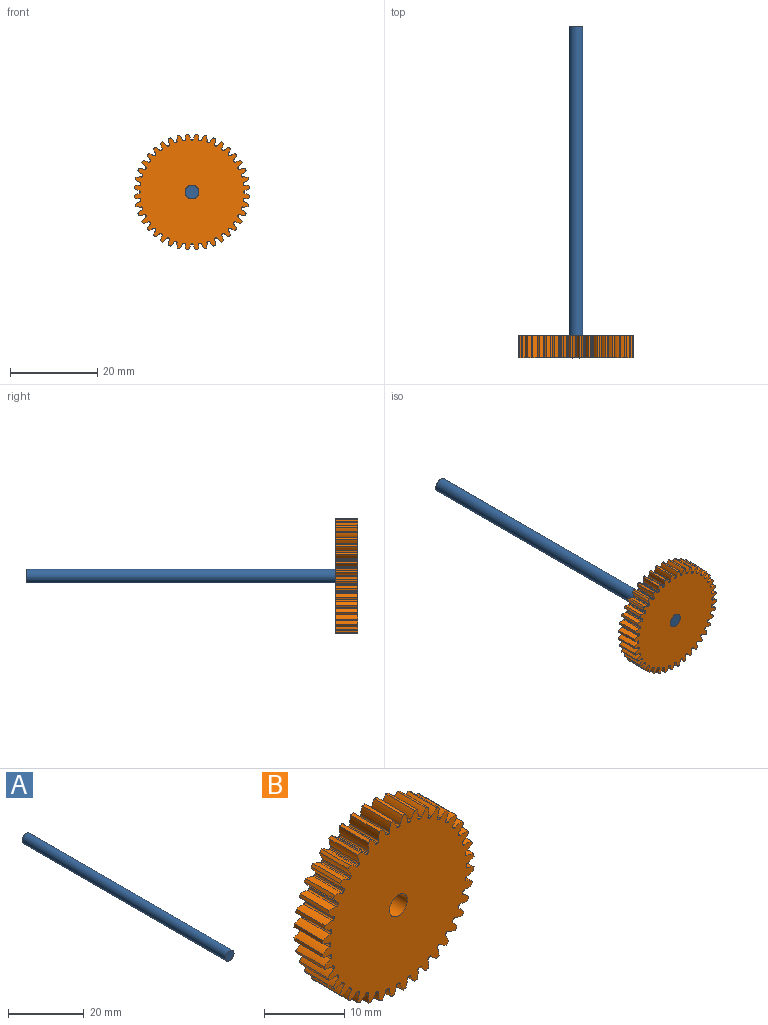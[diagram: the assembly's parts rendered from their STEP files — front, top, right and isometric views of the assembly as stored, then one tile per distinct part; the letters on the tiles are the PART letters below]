
ASSEMBLY  parts=2 mates=1
PART A: 3 faces, bbox 3.2x76.2x3.2 mm
  f0: cylinder r=1.59mm len=76.2mm, axis (0,1,0), area 760.1mm2, adj f1,f2
  f1: plane 3.18x3.18mm, normal (0,-1,0), area 7.9mm2, adj f0
  f2: plane 3.18x3.18mm, normal (0,1,0), area 7.9mm2, adj f0
PART B: 243 faces, bbox 26.6x5.1x26.6 mm
  f0: cylinder r=13.33mm len=5.08mm, axis (0,1,0), area 2.5mm2, adj f39,f41,f147,f239
  f1: cylinder r=13.33mm len=5.08mm, axis (0,1,0), area 2.5mm2, adj f39,f41,f234,f237
  f2: cylinder r=13.33mm len=5.08mm, axis (0,1,0), area 2.5mm2, adj f39,f41,f229,f232
  f3: cylinder r=13.33mm len=5.08mm, axis (0,1,0), area 2.5mm2, adj f39,f41,f224,f227
  f4: cylinder r=13.33mm len=5.08mm, axis (0,1,0), area 2.5mm2, adj f39,f41,f219,f222
  f5: cylinder r=13.33mm len=5.08mm, axis (0,1,0), area 2.5mm2, adj f39,f41,f214,f217
  f6: cylinder r=13.33mm len=5.08mm, axis (0,1,0), area 2.5mm2, adj f39,f41,f209,f212
  f7: cylinder r=13.33mm len=5.08mm, axis (0,1,0), area 2.5mm2, adj f39,f41,f204,f207
  f8: cylinder r=13.33mm len=5.08mm, axis (0,1,0), area 2.5mm2, adj f39,f41,f192,f199
  f9: cylinder r=13.33mm len=5.08mm, axis (0,1,0), area 2.5mm2, adj f39,f41,f194,f202
  f10: cylinder r=13.33mm len=5.08mm, axis (0,1,0), area 2.5mm2, adj f39,f41,f189,f197
  f11: cylinder r=13.33mm len=5.08mm, axis (0,1,0), area 2.5mm2, adj f39,f41,f184,f187
  f12: cylinder r=13.33mm len=5.08mm, axis (0,1,0), area 2.5mm2, adj f39,f41,f179,f182
  f13: cylinder r=13.33mm len=5.08mm, axis (0,1,0), area 2.5mm2, adj f39,f41,f174,f177
  f14: cylinder r=13.33mm len=5.08mm, axis (0,1,0), area 2.5mm2, adj f39,f41,f169,f172
  f15: cylinder r=13.33mm len=5.08mm, axis (0,1,0), area 2.5mm2, adj f39,f41,f164,f167
  f16: cylinder r=13.33mm len=5.08mm, axis (0,1,0), area 2.5mm2, adj f39,f41,f137,f159
  f17: cylinder r=13.33mm len=5.08mm, axis (0,1,0), area 2.5mm2, adj f39,f41,f154,f157
  f18: cylinder r=13.33mm len=5.08mm, axis (0,1,0), area 2.5mm2, adj f39,f41,f142,f149
  f19: cylinder r=13.33mm len=5.08mm, axis (0,1,0), area 2.5mm2, adj f39,f41,f144,f152
  f20: cylinder r=13.33mm len=5.08mm, axis (0,1,0), area 2.5mm2, adj f39,f41,f132,f139
  f21: cylinder r=13.33mm len=5.08mm, axis (0,1,0), area 2.5mm2, adj f39,f41,f127,f134
  f22: cylinder r=13.33mm len=5.08mm, axis (0,1,0), area 2.5mm2, adj f39,f41,f122,f129
  f23: cylinder r=13.33mm len=5.08mm, axis (0,1,0), area 2.5mm2, adj f39,f41,f82,f124
  f24: cylinder r=13.33mm len=5.08mm, axis (0,1,0), area 2.5mm2, adj f39,f41,f42,f119
  f25: cylinder r=13.33mm len=5.08mm, axis (0,1,0), area 2.5mm2, adj f39,f41,f114,f117
  f26: cylinder r=13.33mm len=5.08mm, axis (0,1,0), area 2.5mm2, adj f39,f41,f109,f112
  f27: cylinder r=13.33mm len=5.08mm, axis (0,1,0), area 2.5mm2, adj f39,f41,f104,f107
  f28: cylinder r=13.33mm len=5.08mm, axis (0,1,0), area 2.5mm2, adj f39,f41,f92,f99
  f29: cylinder r=13.33mm len=5.08mm, axis (0,1,0), area 2.5mm2, adj f39,f41,f94,f102
  f30: cylinder r=13.33mm len=5.08mm, axis (0,1,0), area 2.5mm2, adj f39,f41,f89,f97
  f31: cylinder r=13.33mm len=5.08mm, axis (0,1,0), area 2.5mm2, adj f39,f41,f84,f87
  f32: cylinder r=13.33mm len=5.08mm, axis (0,1,0), area 2.5mm2, adj f39,f41,f67,f79
  f33: cylinder r=13.33mm len=5.08mm, axis (0,1,0), area 2.5mm2, adj f39,f41,f74,f77
  f34: cylinder r=13.33mm len=5.08mm, axis (0,1,0), area 2.5mm2, adj f39,f41,f62,f69
  f35: cylinder r=13.33mm len=5.08mm, axis (0,1,0), area 2.5mm2, adj f39,f41,f64,f162
  f36: cylinder r=13.33mm len=5.08mm, axis (0,1,0), area 2.5mm2, adj f39,f41,f59,f72
  f37: cylinder r=13.33mm len=5.08mm, axis (0,1,0), area 2.5mm2, adj f39,f41,f54,f57
  f38: cylinder r=13.33mm len=5.08mm, axis (0,1,0), area 2.5mm2, adj f39,f41,f49,f52
  f39: plane 26.62x26.62mm, normal (0,-1,0), area 495mm2, adj f0,f1,f2,f3,f4,f5,f6,f7
  f40: cylinder r=13.33mm len=5.08mm, axis (0,1,0), area 2.5mm2, adj f39,f41,f44,f47
  f41: plane 26.62x26.62mm, normal (0,1,0), area 495mm2, adj f0,f1,f2,f3,f4,f5,f6,f7
  f42: extruded ~5.08x1.22mm, area 6.7mm2, adj f24,f39,f41,f45
  f43: cylinder r=11.91mm len=5.08mm, axis (0,1,0), area 0.9mm2, adj f39,f41,f45,f46
  f44: extruded ~5.08x1.22mm, area 6.7mm2, adj f39,f40,f41,f46
  f45: cylinder r=0.22mm len=5.08mm, axis (0,1,0), area 1.6mm2, adj f39,f41,f42,f43
  f46: cylinder r=0.22mm len=5.08mm, axis (0,1,0), area 1.6mm2, adj f39,f41,f43,f44
  f47: extruded ~5.08x1.28mm, area 6.7mm2, adj f39,f40,f41,f50
  f48: cylinder r=11.91mm len=5.08mm, axis (0,1,0), area 0.9mm2, adj f39,f41,f50,f51
  f49: extruded ~5.08x1.13mm, area 6.7mm2, adj f38,f39,f41,f51
  f50: cylinder r=0.22mm len=5.08mm, axis (0,1,0), area 1.6mm2, adj f39,f41,f47,f48
  f51: cylinder r=0.22mm len=5.08mm, axis (0,1,0), area 1.6mm2, adj f39,f41,f48,f49
  f52: extruded ~5.08x1.31mm, area 6.7mm2, adj f38,f39,f41,f55
  f53: cylinder r=11.91mm len=5.08mm, axis (0,1,0), area 0.9mm2, adj f39,f41,f55,f56
  f54: extruded ~5.08x1.01mm, area 6.7mm2, adj f37,f39,f41,f56
  f55: cylinder r=0.22mm len=5.08mm, axis (0,1,0), area 1.6mm2, adj f39,f41,f52,f53
  f56: cylinder r=0.22mm len=5.08mm, axis (0,1,0), area 1.6mm2, adj f39,f41,f53,f54
  f57: extruded ~5.08x1.31mm, area 6.7mm2, adj f37,f39,f41,f60
  f58: cylinder r=11.91mm len=5.08mm, axis (0,1,0), area 0.9mm2, adj f39,f41,f60,f61
  f59: extruded ~5.08x0.99mm, area 6.7mm2, adj f36,f39,f41,f61
  f60: cylinder r=0.22mm len=5.08mm, axis (0,1,0), area 1.6mm2, adj f39,f41,f57,f58
  f61: cylinder r=0.22mm len=5.08mm, axis (0,1,0), area 1.6mm2, adj f39,f41,f58,f59
  f62: extruded ~5.08x0.99mm, area 6.7mm2, adj f34,f39,f41,f65
  f63: cylinder r=11.91mm len=5.08mm, axis (0,1,0), area 0.9mm2, adj f39,f41,f65,f66
  f64: extruded ~5.08x1.31mm, area 6.7mm2, adj f35,f39,f41,f66
  f65: cylinder r=0.22mm len=5.08mm, axis (0,1,0), area 1.6mm2, adj f39,f41,f62,f63
  f66: cylinder r=0.22mm len=5.08mm, axis (0,1,0), area 1.6mm2, adj f39,f41,f63,f64
  f67: extruded ~5.08x1.12mm, area 6.7mm2, adj f32,f39,f41,f70
  f68: cylinder r=11.91mm len=5.08mm, axis (0,1,0), area 0.9mm2, adj f39,f41,f70,f71
  f69: extruded ~5.08x1.28mm, area 6.7mm2, adj f34,f39,f41,f71
  f70: cylinder r=0.22mm len=5.08mm, axis (0,1,0), area 1.6mm2, adj f39,f41,f67,f68
  f71: cylinder r=0.22mm len=5.08mm, axis (0,1,0), area 1.6mm2, adj f39,f41,f68,f69
  f72: extruded ~5.08x1.28mm, area 6.7mm2, adj f36,f39,f41,f75
  f73: cylinder r=11.91mm len=5.08mm, axis (0,1,0), area 0.9mm2, adj f39,f41,f75,f76
  f74: extruded ~5.08x1.12mm, area 6.7mm2, adj f33,f39,f41,f76
  f75: cylinder r=0.22mm len=5.08mm, axis (0,1,0), area 1.6mm2, adj f39,f41,f72,f73
  f76: cylinder r=0.22mm len=5.08mm, axis (0,1,0), area 1.6mm2, adj f39,f41,f73,f74
  f77: extruded ~5.08x1.21mm, area 6.7mm2, adj f33,f39,f41,f80
  f78: cylinder r=11.91mm len=5.08mm, axis (0,1,0), area 0.9mm2, adj f39,f41,f80,f81
  f79: extruded ~5.08x1.21mm, area 6.7mm2, adj f32,f39,f41,f81
  f80: cylinder r=0.22mm len=5.08mm, axis (0,1,0), area 1.6mm2, adj f39,f41,f77,f78
  f81: cylinder r=0.22mm len=5.08mm, axis (0,1,0), area 1.6mm2, adj f39,f41,f78,f79
  f82: extruded ~5.08x1.31mm, area 6.7mm2, adj f23,f39,f41,f85
  f83: cylinder r=11.91mm len=5.08mm, axis (0,1,0), area 0.9mm2, adj f39,f41,f85,f86
  f84: extruded ~5.08x1.01mm, area 6.7mm2, adj f31,f39,f41,f86
  f85: cylinder r=0.22mm len=5.08mm, axis (0,1,0), area 1.6mm2, adj f39,f41,f82,f83
  f86: cylinder r=0.22mm len=5.08mm, axis (0,1,0), area 1.6mm2, adj f39,f41,f83,f84
  f87: extruded ~5.08x1.31mm, area 6.7mm2, adj f31,f39,f41,f90
  f88: cylinder r=11.91mm len=5.08mm, axis (0,1,0), area 0.9mm2, adj f39,f41,f90,f91
  f89: extruded ~5.08x0.99mm, area 6.7mm2, adj f30,f39,f41,f91
  f90: cylinder r=0.22mm len=5.08mm, axis (0,1,0), area 1.6mm2, adj f39,f41,f87,f88
  f91: cylinder r=0.22mm len=5.08mm, axis (0,1,0), area 1.6mm2, adj f39,f41,f88,f89
  f92: extruded ~5.08x1.21mm, area 6.7mm2, adj f28,f39,f41,f95
  f93: cylinder r=11.91mm len=5.08mm, axis (0,1,0), area 0.9mm2, adj f39,f41,f95,f96
  f94: extruded ~5.08x1.21mm, area 6.7mm2, adj f29,f39,f41,f96
  f95: cylinder r=0.22mm len=5.08mm, axis (0,1,0), area 1.6mm2, adj f39,f41,f92,f93
  f96: cylinder r=0.22mm len=5.08mm, axis (0,1,0), area 1.6mm2, adj f39,f41,f93,f94
  f97: extruded ~5.08x1.28mm, area 6.7mm2, adj f30,f39,f41,f100
  f98: cylinder r=11.91mm len=5.08mm, axis (0,1,0), area 0.9mm2, adj f39,f41,f100,f101
  f99: extruded ~5.08x1.12mm, area 6.7mm2, adj f28,f39,f41,f101
  f100: cylinder r=0.22mm len=5.08mm, axis (0,1,0), area 1.6mm2, adj f39,f41,f97,f98
  f101: cylinder r=0.22mm len=5.08mm, axis (0,1,0), area 1.6mm2, adj f39,f41,f98,f99
  f102: extruded ~5.08x1.12mm, area 6.7mm2, adj f29,f39,f41,f105
  f103: cylinder r=11.91mm len=5.08mm, axis (0,1,0), area 0.9mm2, adj f39,f41,f105,f106
  f104: extruded ~5.08x1.28mm, area 6.7mm2, adj f27,f39,f41,f106
  f105: cylinder r=0.22mm len=5.08mm, axis (0,1,0), area 1.6mm2, adj f39,f41,f102,f103
  f106: cylinder r=0.22mm len=5.08mm, axis (0,1,0), area 1.6mm2, adj f39,f41,f103,f104
  f107: extruded ~5.08x0.99mm, area 6.7mm2, adj f27,f39,f41,f110
  f108: cylinder r=11.91mm len=5.08mm, axis (0,1,0), area 0.9mm2, adj f39,f41,f110,f111
  f109: extruded ~5.08x1.31mm, area 6.7mm2, adj f26,f39,f41,f111
  f110: cylinder r=0.22mm len=5.08mm, axis (0,1,0), area 1.6mm2, adj f39,f41,f107,f108
  f111: cylinder r=0.22mm len=5.08mm, axis (0,1,0), area 1.6mm2, adj f39,f41,f108,f109
  f112: extruded ~5.08x1.01mm, area 6.7mm2, adj f26,f39,f41,f115
  f113: cylinder r=11.91mm len=5.08mm, axis (0,1,0), area 0.9mm2, adj f39,f41,f115,f116
  f114: extruded ~5.08x1.31mm, area 6.7mm2, adj f25,f39,f41,f116
  f115: cylinder r=0.22mm len=5.08mm, axis (0,1,0), area 1.6mm2, adj f39,f41,f112,f113
  f116: cylinder r=0.22mm len=5.08mm, axis (0,1,0), area 1.6mm2, adj f39,f41,f113,f114
  f117: extruded ~5.08x1.13mm, area 6.7mm2, adj f25,f39,f41,f120
  f118: cylinder r=11.91mm len=5.08mm, axis (0,1,0), area 0.9mm2, adj f39,f41,f120,f121
  f119: extruded ~5.08x1.28mm, area 6.7mm2, adj f24,f39,f41,f121
  f120: cylinder r=0.22mm len=5.08mm, axis (0,1,0), area 1.6mm2, adj f39,f41,f117,f118
  f121: cylinder r=0.22mm len=5.08mm, axis (0,1,0), area 1.6mm2, adj f39,f41,f118,f119
  f122: extruded ~5.08x1.28mm, area 6.7mm2, adj f22,f39,f41,f125
  f123: cylinder r=11.91mm len=5.08mm, axis (0,1,0), area 0.9mm2, adj f39,f41,f125,f126
  f124: extruded ~5.08x1.13mm, area 6.7mm2, adj f23,f39,f41,f126
  f125: cylinder r=0.22mm len=5.08mm, axis (0,1,0), area 1.6mm2, adj f39,f41,f122,f123
  f126: cylinder r=0.22mm len=5.08mm, axis (0,1,0), area 1.6mm2, adj f39,f41,f123,f124
  f127: extruded ~5.08x1.22mm, area 6.7mm2, adj f21,f39,f41,f130
  f128: cylinder r=11.91mm len=5.08mm, axis (0,1,0), area 0.9mm2, adj f39,f41,f130,f131
  f129: extruded ~5.08x1.22mm, area 6.7mm2, adj f22,f39,f41,f131
  f130: cylinder r=0.22mm len=5.08mm, axis (0,1,0), area 1.6mm2, adj f39,f41,f127,f128
  f131: cylinder r=0.22mm len=5.08mm, axis (0,1,0), area 1.6mm2, adj f39,f41,f128,f129
  f132: extruded ~5.08x1.13mm, area 6.7mm2, adj f20,f39,f41,f135
  f133: cylinder r=11.91mm len=5.08mm, axis (0,1,0), area 0.9mm2, adj f39,f41,f135,f136
  f134: extruded ~5.08x1.28mm, area 6.7mm2, adj f21,f39,f41,f136
  f135: cylinder r=0.22mm len=5.08mm, axis (0,1,0), area 1.6mm2, adj f39,f41,f132,f133
  f136: cylinder r=0.22mm len=5.08mm, axis (0,1,0), area 1.6mm2, adj f39,f41,f133,f134
  f137: extruded ~5.08x1.01mm, area 6.7mm2, adj f16,f39,f41,f140
  f138: cylinder r=11.91mm len=5.08mm, axis (0,1,0), area 0.9mm2, adj f39,f41,f140,f141
  f139: extruded ~5.08x1.31mm, area 6.7mm2, adj f20,f39,f41,f141
  f140: cylinder r=0.22mm len=5.08mm, axis (0,1,0), area 1.6mm2, adj f39,f41,f137,f138
  f141: cylinder r=0.22mm len=5.08mm, axis (0,1,0), area 1.6mm2, adj f39,f41,f138,f139
  f142: extruded ~5.08x1.21mm, area 6.7mm2, adj f18,f39,f41,f145
  f143: cylinder r=11.91mm len=5.08mm, axis (0,1,0), area 0.9mm2, adj f39,f41,f145,f146
  f144: extruded ~5.08x1.21mm, area 6.7mm2, adj f19,f39,f41,f146
  f145: cylinder r=0.22mm len=5.08mm, axis (0,1,0), area 1.6mm2, adj f39,f41,f142,f143
  f146: cylinder r=0.22mm len=5.08mm, axis (0,1,0), area 1.6mm2, adj f39,f41,f143,f144
  f147: extruded ~5.08x1.28mm, area 6.7mm2, adj f0,f39,f41,f150
  f148: cylinder r=11.91mm len=5.08mm, axis (0,1,0), area 0.9mm2, adj f39,f41,f150,f151
  f149: extruded ~5.08x1.12mm, area 6.7mm2, adj f18,f39,f41,f151
  f150: cylinder r=0.22mm len=5.08mm, axis (0,1,0), area 1.6mm2, adj f39,f41,f147,f148
  f151: cylinder r=0.22mm len=5.08mm, axis (0,1,0), area 1.6mm2, adj f39,f41,f148,f149
  f152: extruded ~5.08x1.12mm, area 6.7mm2, adj f19,f39,f41,f155
  f153: cylinder r=11.91mm len=5.08mm, axis (0,1,0), area 0.9mm2, adj f39,f41,f155,f156
  f154: extruded ~5.08x1.28mm, area 6.7mm2, adj f17,f39,f41,f156
  f155: cylinder r=0.22mm len=5.08mm, axis (0,1,0), area 1.6mm2, adj f39,f41,f152,f153
  f156: cylinder r=0.22mm len=5.08mm, axis (0,1,0), area 1.6mm2, adj f39,f41,f153,f154
  f157: extruded ~5.08x0.99mm, area 6.7mm2, adj f17,f39,f41,f160
  f158: cylinder r=11.91mm len=5.08mm, axis (0,1,0), area 0.9mm2, adj f39,f41,f160,f161
  f159: extruded ~5.08x1.31mm, area 6.7mm2, adj f16,f39,f41,f161
  f160: cylinder r=0.22mm len=5.08mm, axis (0,1,0), area 1.6mm2, adj f39,f41,f157,f158
  f161: cylinder r=0.22mm len=5.08mm, axis (0,1,0), area 1.6mm2, adj f39,f41,f158,f159
  f162: extruded ~5.08x1.01mm, area 6.7mm2, adj f35,f39,f41,f165
  f163: cylinder r=11.91mm len=5.08mm, axis (0,1,0), area 0.9mm2, adj f39,f41,f165,f166
  f164: extruded ~5.08x1.31mm, area 6.7mm2, adj f15,f39,f41,f166
  f165: cylinder r=0.22mm len=5.08mm, axis (0,1,0), area 1.6mm2, adj f39,f41,f162,f163
  f166: cylinder r=0.22mm len=5.08mm, axis (0,1,0), area 1.6mm2, adj f39,f41,f163,f164
  f167: extruded ~5.08x1.13mm, area 6.7mm2, adj f15,f39,f41,f170
  f168: cylinder r=11.91mm len=5.08mm, axis (0,1,0), area 0.9mm2, adj f39,f41,f170,f171
  f169: extruded ~5.08x1.28mm, area 6.7mm2, adj f14,f39,f41,f171
  f170: cylinder r=0.22mm len=5.08mm, axis (0,1,0), area 1.6mm2, adj f39,f41,f167,f168
  f171: cylinder r=0.22mm len=5.08mm, axis (0,1,0), area 1.6mm2, adj f39,f41,f168,f169
  f172: extruded ~5.08x1.22mm, area 6.7mm2, adj f14,f39,f41,f175
  f173: cylinder r=11.91mm len=5.08mm, axis (0,1,0), area 0.9mm2, adj f39,f41,f175,f176
  f174: extruded ~5.08x1.22mm, area 6.7mm2, adj f13,f39,f41,f176
  f175: cylinder r=0.22mm len=5.08mm, axis (0,1,0), area 1.6mm2, adj f39,f41,f172,f173
  f176: cylinder r=0.22mm len=5.08mm, axis (0,1,0), area 1.6mm2, adj f39,f41,f173,f174
  f177: extruded ~5.08x1.28mm, area 6.7mm2, adj f13,f39,f41,f180
  f178: cylinder r=11.91mm len=5.08mm, axis (0,1,0), area 0.9mm2, adj f39,f41,f180,f181
  f179: extruded ~5.08x1.13mm, area 6.7mm2, adj f12,f39,f41,f181
  f180: cylinder r=0.22mm len=5.08mm, axis (0,1,0), area 1.6mm2, adj f39,f41,f177,f178
  f181: cylinder r=0.22mm len=5.08mm, axis (0,1,0), area 1.6mm2, adj f39,f41,f178,f179
  f182: extruded ~5.08x1.31mm, area 6.7mm2, adj f12,f39,f41,f185
  f183: cylinder r=11.91mm len=5.08mm, axis (0,1,0), area 0.9mm2, adj f39,f41,f185,f186
  f184: extruded ~5.08x1.01mm, area 6.7mm2, adj f11,f39,f41,f186
  f185: cylinder r=0.22mm len=5.08mm, axis (0,1,0), area 1.6mm2, adj f39,f41,f182,f183
  f186: cylinder r=0.22mm len=5.08mm, axis (0,1,0), area 1.6mm2, adj f39,f41,f183,f184
  f187: extruded ~5.08x1.31mm, area 6.7mm2, adj f11,f39,f41,f190
  f188: cylinder r=11.91mm len=5.08mm, axis (0,1,0), area 0.9mm2, adj f39,f41,f190,f191
  f189: extruded ~5.08x0.99mm, area 6.7mm2, adj f10,f39,f41,f191
  f190: cylinder r=0.22mm len=5.08mm, axis (0,1,0), area 1.6mm2, adj f39,f41,f187,f188
  f191: cylinder r=0.22mm len=5.08mm, axis (0,1,0), area 1.6mm2, adj f39,f41,f188,f189
  f192: extruded ~5.08x1.21mm, area 6.7mm2, adj f8,f39,f41,f195
  f193: cylinder r=11.91mm len=5.08mm, axis (0,1,0), area 0.9mm2, adj f39,f41,f195,f196
  f194: extruded ~5.08x1.21mm, area 6.7mm2, adj f9,f39,f41,f196
  f195: cylinder r=0.22mm len=5.08mm, axis (0,1,0), area 1.6mm2, adj f39,f41,f192,f193
  f196: cylinder r=0.22mm len=5.08mm, axis (0,1,0), area 1.6mm2, adj f39,f41,f193,f194
  f197: extruded ~5.08x1.28mm, area 6.7mm2, adj f10,f39,f41,f200
  f198: cylinder r=11.91mm len=5.08mm, axis (0,1,0), area 0.9mm2, adj f39,f41,f200,f201
  f199: extruded ~5.08x1.12mm, area 6.7mm2, adj f8,f39,f41,f201
  f200: cylinder r=0.22mm len=5.08mm, axis (0,1,0), area 1.6mm2, adj f39,f41,f197,f198
  f201: cylinder r=0.22mm len=5.08mm, axis (0,1,0), area 1.6mm2, adj f39,f41,f198,f199
  f202: extruded ~5.08x1.12mm, area 6.7mm2, adj f9,f39,f41,f205
  f203: cylinder r=11.91mm len=5.08mm, axis (0,1,0), area 0.9mm2, adj f39,f41,f205,f206
  f204: extruded ~5.08x1.28mm, area 6.7mm2, adj f7,f39,f41,f206
  f205: cylinder r=0.22mm len=5.08mm, axis (0,1,0), area 1.6mm2, adj f39,f41,f202,f203
  f206: cylinder r=0.22mm len=5.08mm, axis (0,1,0), area 1.6mm2, adj f39,f41,f203,f204
  f207: extruded ~5.08x0.99mm, area 6.7mm2, adj f7,f39,f41,f210
  f208: cylinder r=11.91mm len=5.08mm, axis (0,1,0), area 0.9mm2, adj f39,f41,f210,f211
  f209: extruded ~5.08x1.31mm, area 6.7mm2, adj f6,f39,f41,f211
  f210: cylinder r=0.22mm len=5.08mm, axis (0,1,0), area 1.6mm2, adj f39,f41,f207,f208
  f211: cylinder r=0.22mm len=5.08mm, axis (0,1,0), area 1.6mm2, adj f39,f41,f208,f209
  f212: extruded ~5.08x1.01mm, area 6.7mm2, adj f6,f39,f41,f215
  f213: cylinder r=11.91mm len=5.08mm, axis (0,1,0), area 0.9mm2, adj f39,f41,f215,f216
  f214: extruded ~5.08x1.31mm, area 6.7mm2, adj f5,f39,f41,f216
  f215: cylinder r=0.22mm len=5.08mm, axis (0,1,0), area 1.6mm2, adj f39,f41,f212,f213
  f216: cylinder r=0.22mm len=5.08mm, axis (0,1,0), area 1.6mm2, adj f39,f41,f213,f214
  f217: extruded ~5.08x1.13mm, area 6.7mm2, adj f5,f39,f41,f220
  f218: cylinder r=11.91mm len=5.08mm, axis (0,1,0), area 0.9mm2, adj f39,f41,f220,f221
  f219: extruded ~5.08x1.28mm, area 6.7mm2, adj f4,f39,f41,f221
  f220: cylinder r=0.22mm len=5.08mm, axis (0,1,0), area 1.6mm2, adj f39,f41,f217,f218
  f221: cylinder r=0.22mm len=5.08mm, axis (0,1,0), area 1.6mm2, adj f39,f41,f218,f219
  f222: extruded ~5.08x1.22mm, area 6.7mm2, adj f4,f39,f41,f225
  f223: cylinder r=11.91mm len=5.08mm, axis (0,1,0), area 0.9mm2, adj f39,f41,f225,f226
  f224: extruded ~5.08x1.22mm, area 6.7mm2, adj f3,f39,f41,f226
  f225: cylinder r=0.22mm len=5.08mm, axis (0,1,0), area 1.6mm2, adj f39,f41,f222,f223
  f226: cylinder r=0.22mm len=5.08mm, axis (0,1,0), area 1.6mm2, adj f39,f41,f223,f224
  f227: extruded ~5.08x1.28mm, area 6.7mm2, adj f3,f39,f41,f230
  f228: cylinder r=11.91mm len=5.08mm, axis (0,1,0), area 0.9mm2, adj f39,f41,f230,f231
  f229: extruded ~5.08x1.13mm, area 6.7mm2, adj f2,f39,f41,f231
  f230: cylinder r=0.22mm len=5.08mm, axis (0,1,0), area 1.6mm2, adj f39,f41,f227,f228
  f231: cylinder r=0.22mm len=5.08mm, axis (0,1,0), area 1.6mm2, adj f39,f41,f228,f229
  f232: extruded ~5.08x1.31mm, area 6.7mm2, adj f2,f39,f41,f235
  f233: cylinder r=11.91mm len=5.08mm, axis (0,1,0), area 0.9mm2, adj f39,f41,f235,f236
  f234: extruded ~5.08x1.01mm, area 6.7mm2, adj f1,f39,f41,f236
  f235: cylinder r=0.22mm len=5.08mm, axis (0,1,0), area 1.6mm2, adj f39,f41,f232,f233
  f236: cylinder r=0.22mm len=5.08mm, axis (0,1,0), area 1.6mm2, adj f39,f41,f233,f234
  f237: extruded ~5.08x1.31mm, area 6.7mm2, adj f1,f39,f41,f240
  f238: cylinder r=11.91mm len=5.08mm, axis (0,1,0), area 0.9mm2, adj f39,f41,f240,f241
  f239: extruded ~5.08x0.99mm, area 6.7mm2, adj f0,f39,f41,f241
  f240: cylinder r=0.22mm len=5.08mm, axis (0,1,0), area 1.6mm2, adj f39,f41,f237,f238
  f241: cylinder r=0.22mm len=5.08mm, axis (0,1,0), area 1.6mm2, adj f39,f41,f238,f239
  f242: cylinder r=1.59mm len=5.08mm, axis (0,1,0), area 50.7mm2, adj f39,f41
PLACE A t=(47.88,75.91,-54.84)mm
PLACE B t=(-11.39,4.79,-16.38)mm
MATE fastened A.f0 <-> B.f0  axis (0,-1,0) through (-11.39,-0.29,-16.38)mm
